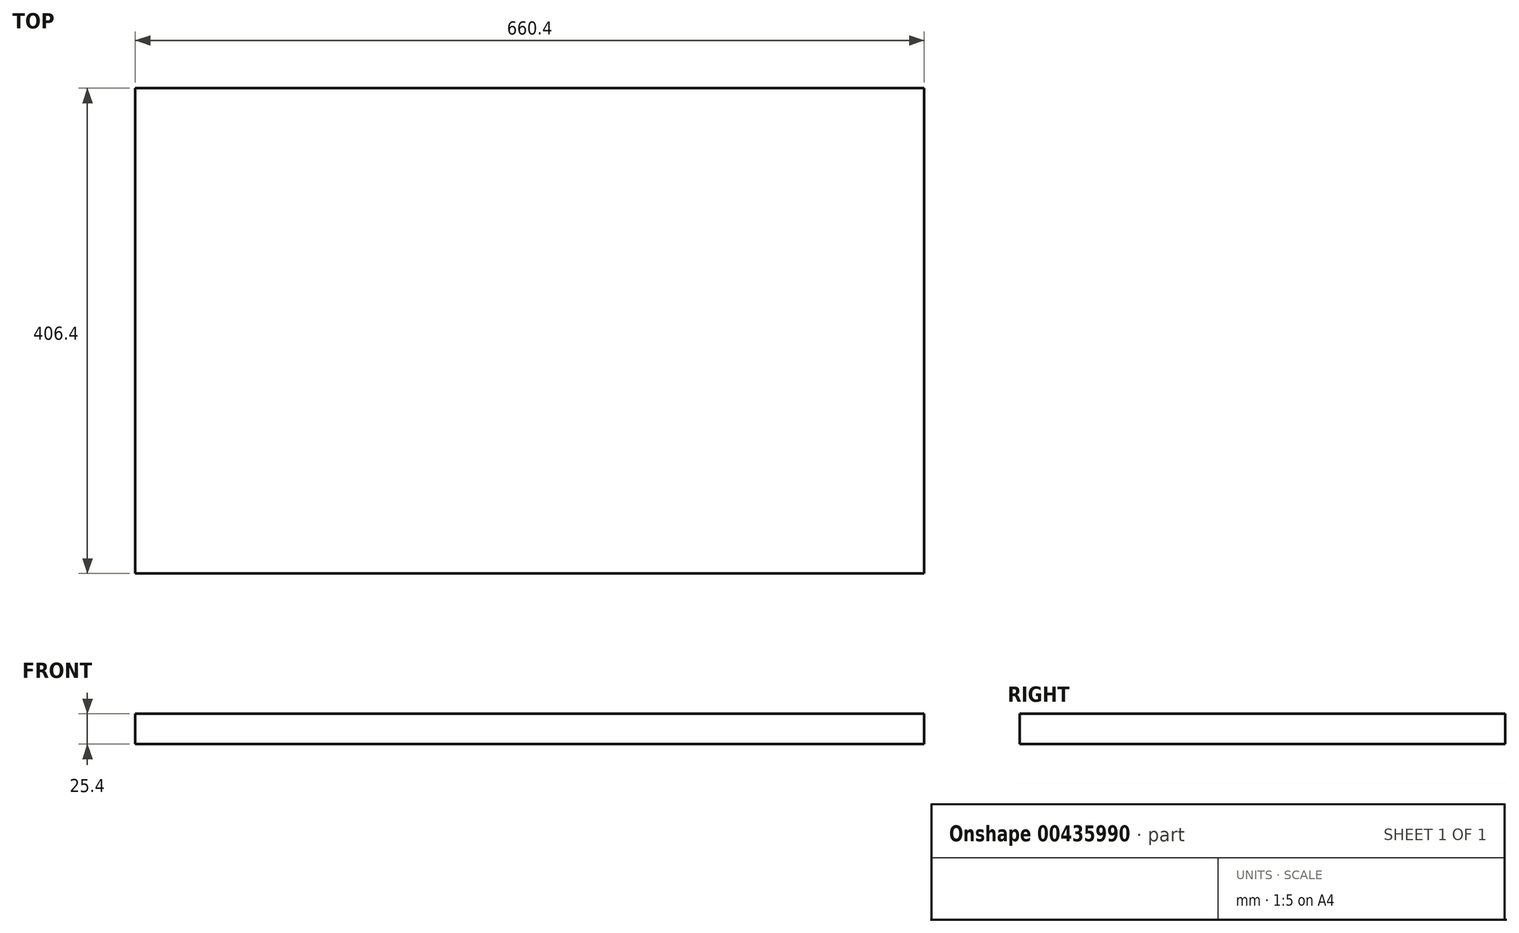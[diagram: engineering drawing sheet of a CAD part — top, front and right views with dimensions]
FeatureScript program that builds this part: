
annotation { "Feature Type Name" : "Feature", "Feature Type Description" : "" }
export const myFeature = defineFeature(function(context is Context, id is Id, definition is map)
    precondition{}
    {
        {
            var Q0;
            Q0=qCreatedBy(makeId("Front.planeOp"),FACE);
            var sketch = newSketch(context, id + "F0", { "sketchPlane" : qUnion([Q0])});
            skLineSegment(sketch, "E0.bottom", {"start": v(-294.22, 25.4) * mm, "end": v(366.18, 25.4) * mm});
            skLineSegment(sketch, "E0.top", {"start": v(-294.22, 0) * mm, "end": v(366.18, 0) * mm});
            skLineSegment(sketch, "E0.left", {"start": v(-294.22, 25.4) * mm, "end": v(-294.22, 0) * mm});
            skLineSegment(sketch, "E0.right", {"start": v(366.18, 25.4) * mm, "end": v(366.18, 0) * mm});
            skSolve(sketch);
        }
        {
            var Q0;
            Q0=makeQuery(id+"F0.imprint","IMPRINT",FACE,{"disambiguationData":[TD([[makeQuery(id+"F0.imprint","IMPRINT",EDGE,{"derivedFrom":sQuery(id+"F0.wireOp",EDGE,"E0.bottom")}),-1.0]])]});
            extrude(context, id + "F1", {"entities" : qUnion([Q0]), "depth" : 406.4 * mm});
        }
    });
